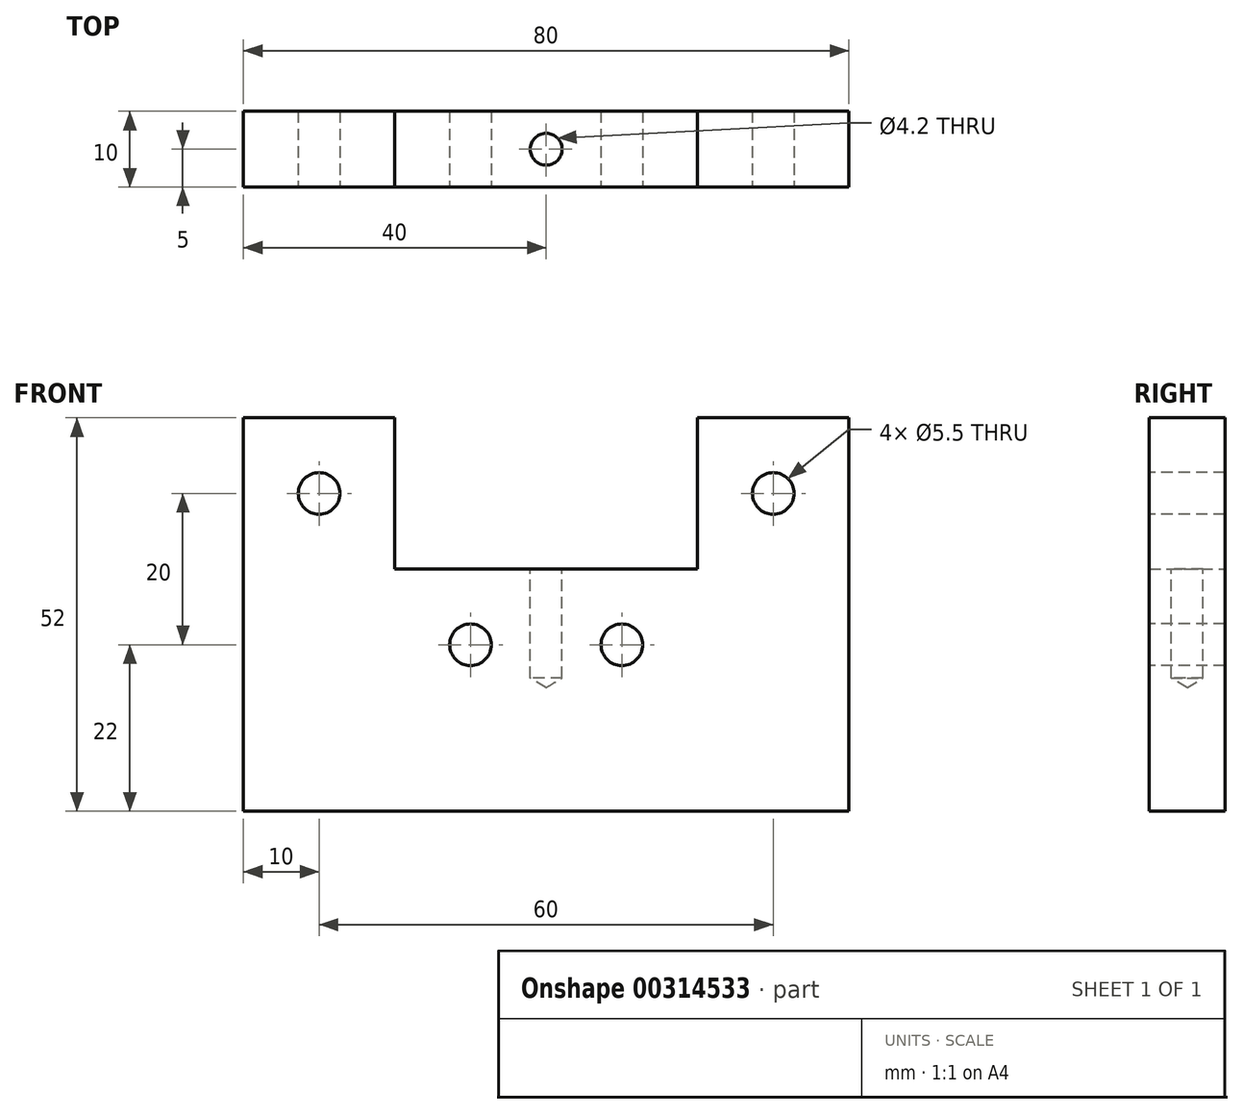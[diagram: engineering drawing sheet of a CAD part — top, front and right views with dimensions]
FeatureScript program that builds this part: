
annotation { "Feature Type Name" : "Feature", "Feature Type Description" : "" }
export const myFeature = defineFeature(function(context is Context, id is Id, definition is map)
    precondition{}
    {
        {
            var Q0;
            Q0=qCreatedBy(makeId("Front.planeOp"),FACE);
            var sketch = newSketch(context, id + "F0", { "sketchPlane" : qUnion([Q0])});
            skLineSegment(sketch, "E0.bottom", {"start": v(-40, -26) * mm, "end": v(40, -26) * mm});
            skLineSegment(sketch, "E0.top", {"start": v(-40, 26) * mm, "end": v(-20, 26) * mm});
            skLineSegment(sketch, "E0.left", {"start": v(-40, -26) * mm, "end": v(-40, 26) * mm});
            skLineSegment(sketch, "E0.right", {"start": v(40, -26) * mm, "end": v(40, 26) * mm});
            skPoint(sketch, "E0.middle", {"position": v(0, 0) * mm});
            skLineSegment(sketch, "E1.top", {"start": v(-20, 6) * mm, "end": v(20, 6) * mm});
            skLineSegment(sketch, "E1.left", {"start": v(-20, 26) * mm, "end": v(-20, 6) * mm});
            skLineSegment(sketch, "E1.right", {"start": v(20, 26) * mm, "end": v(20, 6) * mm});
            skLineSegment(sketch, "E2.trimOffspring", {"start": v(20, 26) * mm, "end": v(40, 26) * mm});
            skSolve(sketch);
        }
        {
            var Q0;
            Q0 = qSketchRegion(id + "F0", true);
            extrude(context, id + "F1", {"entities" : qUnion([Q0]), "depth" : 10 * mm});
        }
        {
            var Q0;
            Q0=makeQuery(id+"F1.opExtrude","CAP_FACE",FACE,{"disambiguationData":[OSD([sQuery(id+"F0.wireOp",EDGE,"E0.bottom"),sQuery(id+"F0.wireOp",EDGE,"E0.top"),sQuery(id+"F0.wireOp",EDGE,"E0.left"),sQuery(id+"F0.wireOp",EDGE,"E0.right"),sQuery(id+"F0.wireOp",EDGE,"E1.top"),sQuery(id+"F0.wireOp",EDGE,"E1.left"),sQuery(id+"F0.wireOp",EDGE,"E1.right"),sQuery(id+"F0.wireOp",EDGE,"E2.trimOffspring")])],"isStart":false});
            var sketch = newSketch(context, id + "F2", { "sketchPlane" : qUnion([Q0])});
            skPoint(sketch, "E3", {"position": v(-30, 16) * mm});
            skPoint(sketch, "E4.MirrorP", {"position": v(30, 16) * mm});
            skPoint(sketch, "E5", {"position": v(-10, -4) * mm});
            skPoint(sketch, "E6.MirrorP", {"position": v(10, -4) * mm});
            skSolve(sketch);
        }
        {
            var Q0;
            Q0=sQuery(id+"F2.wireOp",VERTEX,"E3");
            var Q1;
            Q1=sQuery(id+"F2.wireOp",VERTEX,"E5");
            var Q2;
            Q2=sQuery(id+"F2.wireOp",VERTEX,"E6.MirrorP");
            var Q3;
            Q3=sQuery(id+"F2.wireOp",VERTEX,"E4.MirrorP");
            var Q4;
            Q4=makeQuery(id+"F1.opExtrude","SWEPT_BODY",BODY,{"disambiguationData":[OSD([sQuery(id+"F0.wireOp",EDGE,"E0.bottom"),sQuery(id+"F0.wireOp",EDGE,"E0.top"),sQuery(id+"F0.wireOp",EDGE,"E0.left"),sQuery(id+"F0.wireOp",EDGE,"E0.right"),sQuery(id+"F0.wireOp",EDGE,"E1.top"),sQuery(id+"F0.wireOp",EDGE,"E1.left"),sQuery(id+"F0.wireOp",EDGE,"E1.right"),sQuery(id+"F0.wireOp",EDGE,"E2.trimOffspring")])]});
            hole(context, id + "F3", {"style" : HoleStyle.SIMPLE, "endStyle" : HoleEndStyle.THROUGH, "standardTappedOrClearance" : lookupTablePath({ "standard" : "ISO", "fit" : "Normal", "size" : "M5", "type" : "Clearance" }), "standardBlindInLast" : lookupTablePath({ "fit" : "Standard", "standard" : "ISO", "size" : "M5", "type" : "Clearance" }), "holeDiameter" : 5.5 * mm, "tappedDepth" : 12 * mm, "tapClearance" : 3, "locations" : qUnion([Q0, Q1, Q2, Q3]), "scope" : qUnion([Q4])});
        }
        {
            var Q0;
            Q0=makeQuery(id+"F1.opExtrude","SWEPT_FACE",FACE,{"disambiguationData":[OSD([sQuery(id+"F0.wireOp",EDGE,"E1.top")])]});
            var sketch = newSketch(context, id + "F4", { "sketchPlane" : qUnion([Q0])});
            skPoint(sketch, "E7", {"position": v(0, -5) * mm});
            skPoint(sketch, "E7.positionSnap0", {"position": v(0, -10) * mm});
            skSolve(sketch);
        }
        {
            var Q0;
            Q0=sQuery(id+"F4.wireOp",VERTEX,"E7");
            var Q1;
            Q1=makeQuery(id+"F1.opExtrude","SWEPT_BODY",BODY,{"disambiguationData":[OSD([sQuery(id+"F0.wireOp",EDGE,"E0.bottom"),sQuery(id+"F0.wireOp",EDGE,"E0.top"),sQuery(id+"F0.wireOp",EDGE,"E0.left"),sQuery(id+"F0.wireOp",EDGE,"E0.right"),sQuery(id+"F0.wireOp",EDGE,"E1.top"),sQuery(id+"F0.wireOp",EDGE,"E1.left"),sQuery(id+"F0.wireOp",EDGE,"E1.right"),sQuery(id+"F0.wireOp",EDGE,"E2.trimOffspring")])]});
            hole(context, id + "F5", {"style" : HoleStyle.SIMPLE, "endStyle" : HoleEndStyle.BLIND, "standardTappedOrClearance" : lookupTablePath({ "standard" : "ISO", "engagement" : "75%", "pitch" : "0.8 mm", "size" : "M5", "type" : "Tapped" }), "standardBlindInLast" : lookupTablePath({ "standard" : "ISO", "engagement" : "75%", "pitch" : "0.8 mm", "size" : "M5", "type" : "Tapped" }), "holeDiameter" : 4.2 * mm, "showTappedDepth" : true, "holeDepth" : 14.4 * mm, "tappedDepth" : 12 * mm, "tapClearance" : 3, "locations" : qUnion([Q0]), "scope" : qUnion([Q1]), "majorDiameter" : 5 * mm});
        }
    });
